# Revit family: Ladder_Vertical_KattsafeUSA_Caged_WalkwayPlatform
name_source: partatom
category: Specialty Equipment
units: mm (PartAtom-declared; Revit-internal decimal feet)

## family parameters
Always vertical = Yes
Classification Number = 23.17.23.15
Cut with Voids When Loaded = No
Enable Cutting in Views = No
Maintain Annotation Orientation = No
Part Type = Normal
Room Calculation Point = No
Round Connector Dimension = Use Diameter
Shared = No
Work Plane-Based = No

## types (2) — shared parameters
Angle = 90.00°
Assembly Code = E1090100
Default Elevation = 0' - 0"
ElementType = Ladder
Export Type to IFC As = IfcBuildingElementProxy
IfcExportAs = IfcBuildingElementProxy
IfcExportType = USERDEFINED
Manufacturer = Kattsafe®
ManufacturerOverallWidth = 4' - 7"
ManufacturerURLProductSpecific = https://kattsafe.com
Material = Aluminum_Kattsafe_Satin
ModifiedIssue = 20250822 $
Type IFC Predefined Type = USERDEFINED
URL = https://kattsafe.com
Uniclass2015Code = Pr_25_30_85_02
Uniclass2015Title = Access ladders
Uniclass2015Version = Products v1.35

## per-type parameters (varying)
| type | Description | ManufacturerSpecCode | Model | PlatformLength | Type Comments |
| 3ft (RL45) | Our RL45 model has a 3-foot platform walkway featuring a sturdy aluminum mesh and ribbed finish. We supply it as a kit for on-site sizing and assembly. Customize this design with self-closing platform gates and multiple mounting styles. | RL45 | RL45 | 1' - 7" | Ladder - Caged - 3ft Walkway Platform |
| 8ft (RL43) | We’ve designed the RL33 fixed ladder with an 8-foot walkway at the ladder head for safer access. For extra safety and stability, mesh-style decking and round knee rails surround the platform. Attach knee rails to each post with self-tapping screws and choose from multiple mounting configurations. | RL43 | RL43 | 8' - 0" | Ladder - Caged - 8ft Walkway Platform |

## geometry (parser evidence)
native form markers: Sweep x15
no freeform markers — native parametric forms only
